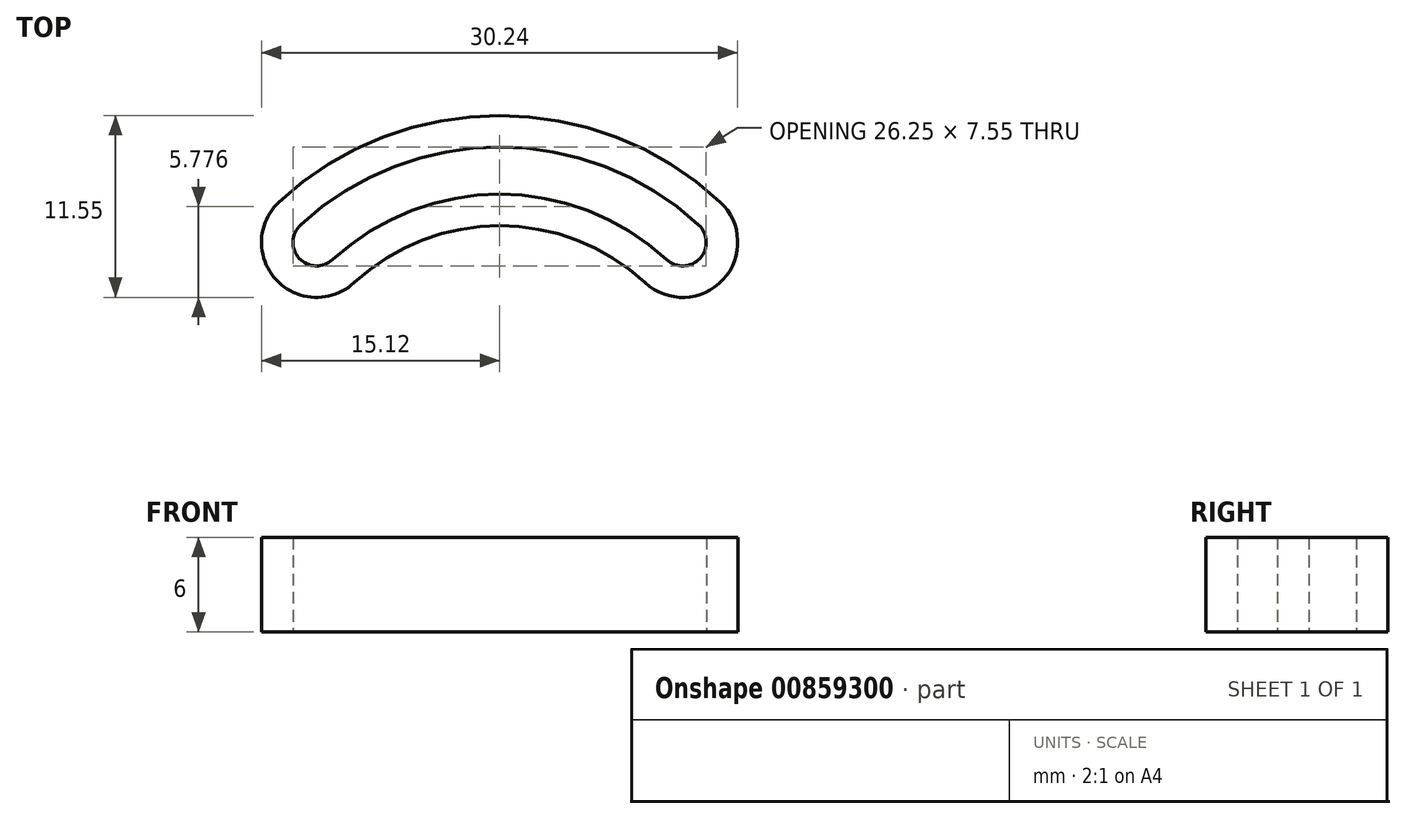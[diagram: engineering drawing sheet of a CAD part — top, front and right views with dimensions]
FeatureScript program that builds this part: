
annotation { "Feature Type Name" : "Feature", "Feature Type Description" : "" }
export const myFeature = defineFeature(function(context is Context, id is Id, definition is map)
    precondition{}
    {
        {
            var Q0;
            Q0=qCreatedBy(makeId("Top.planeOp"),FACE);
            var sketch = newSketch(context, id + "F0", { "sketchPlane" : qUnion([Q0])});
            skArc(sketch, "E0", {"start": v(9.25, 0) * mm, "mid": v(0, 3.62) * mm, "end": v(-9.25, 0) * mm});
            skArc(sketch, "E1", {"start": v(14, 5.14) * mm, "mid": v(0, 10.62) * mm, "end": v(-14, 5.14) * mm});
            skArc(sketch, "E2", {"start": v(-14, 5.14) * mm, "mid": v(-14.2, 0.2) * mm, "end": v(-9.25, 0) * mm});
            skArc(sketch, "E3", {"start": v(9.25, 0) * mm, "mid": v(14.2, 0.2) * mm, "end": v(14, 5.14) * mm});
            skArc(sketch, "E4", {"start": v(11.62, 2.57) * mm, "mid": v(0, 7.12) * mm, "end": v(-11.62, 2.57) * mm});
            skArc(sketch, "E5.0.startCap", {"start": v(12.64, 3.67) * mm, "mid": v(12.73, 1.55) * mm, "end": v(10.6, 1.47) * mm});
            skArc(sketch, "E5.0.endCap", {"start": v(-10.6, 1.47) * mm, "mid": v(-12.73, 1.55) * mm, "end": v(-12.64, 3.67) * mm});
            skArc(sketch, "E5.0.left", {"start": v(10.6, 1.47) * mm, "mid": v(0, 5.62) * mm, "end": v(-10.6, 1.47) * mm});
            skArc(sketch, "E5.0.right", {"start": v(12.64, 3.67) * mm, "mid": v(0, 8.62) * mm, "end": v(-12.64, 3.67) * mm});
            skSolve(sketch);
        }
        {
            var Q0;
            Q0=makeQuery(id+"F0.imprint","IMPRINT",FACE,{"disambiguationData":[TD([[makeQuery(id+"F0.imprint","IMPRINT",EDGE,{"derivedFrom":sQuery(id+"F0.wireOp",EDGE,"E0")}),-1.0]])]});
            extrude(context, id + "F1", {"entities" : qUnion([Q0]), "depth" : 6 * mm, "offsetDistance" : 25 * mm});
        }
    });
